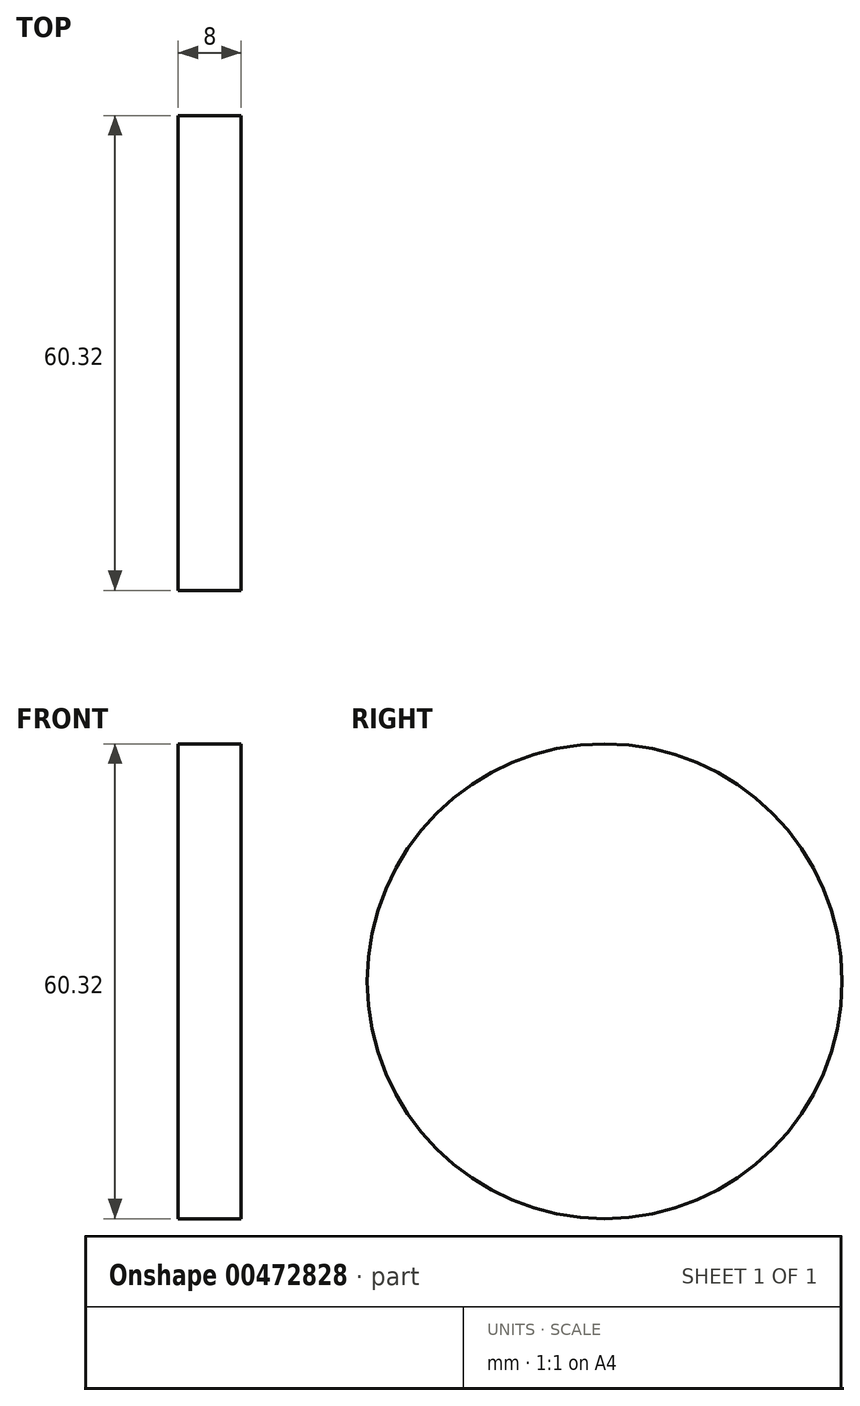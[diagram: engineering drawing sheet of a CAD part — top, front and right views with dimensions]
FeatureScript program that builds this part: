
annotation { "Feature Type Name" : "Feature", "Feature Type Description" : "" }
export const myFeature = defineFeature(function(context is Context, id is Id, definition is map)
    precondition{}
    {
        {
            assignVariable(context, id + "F0", {"name" : "RollerLength", "anyValue" : 8});
        }
        {
            var Q0;
            Q0=qCreatedBy(makeId("Right.planeOp"),FACE);
            var sketch = newSketch(context, id + "F1", { "sketchPlane" : qUnion([Q0])});
            skCircle(sketch, "E0", {"center": v(0, 0) * mm, "radius": 30.16 * mm});
            skSolve(sketch);
        }
        {
            var Q0;
            Q0=makeQuery(id+"F1.imprint","IMPRINT",FACE,{"disambiguationData":[TD([[makeQuery(id+"F1.imprint","IMPRINT",EDGE,{"derivedFrom":sQuery(id+"F1.wireOp",EDGE,"E0")}),1.0]])]});
            extrude(context, id + "F2", {"entities" : qUnion([Q0]), "endBound" : BoundingType.SYMMETRIC, "depth" : (getVariable(context, 'RollerLength')) * mm});
        }
    });
